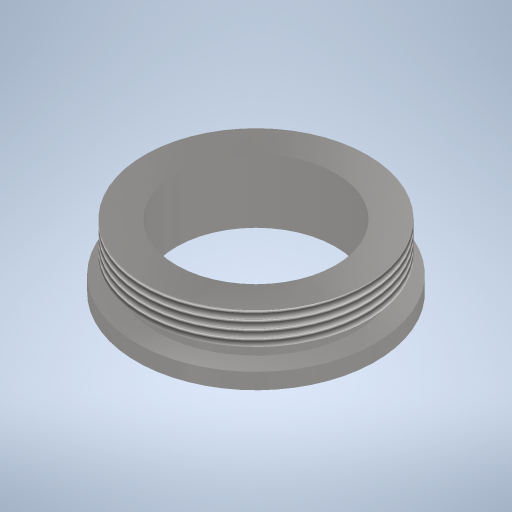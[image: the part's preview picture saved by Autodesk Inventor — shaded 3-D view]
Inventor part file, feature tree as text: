
AUTODESK INVENTOR PART (.ipt)
format: ipt  version: 2023 (Build 270158000, 158)  size: 275,968 bytes
history: native  units: in
note: dims shown in document units (in); Inventor stores cm internally (conversion verified against a paired STEP export)
features: revolve x1, thread x1, sketch x1
ambient origin geometry x8: Origin, YZ Plane, XZ Plane, XY Plane, X Axis, Y Axis, Z Axis, Center Point
bodies: Solid1 (feature_tree)
feature tree (3):
  revolve  "Revolution1"  [1 undecoded]
  thread  "Thread1"  [1 undecoded]
  sketch  "Sketch1"  dims[d0=0.7874in d1=0.2362in d2=0.0787in d3=1.1024in d4=1.1811in d5=360.0deg d6=0.1969in d7=0.0in d8=0.0787in d9=0.0591in]
note: 2 required parameter values undecoded (feature->parameter linkage not recoverable at this tier; creation-order binding heuristic only, values carry confidence <= 0.55)